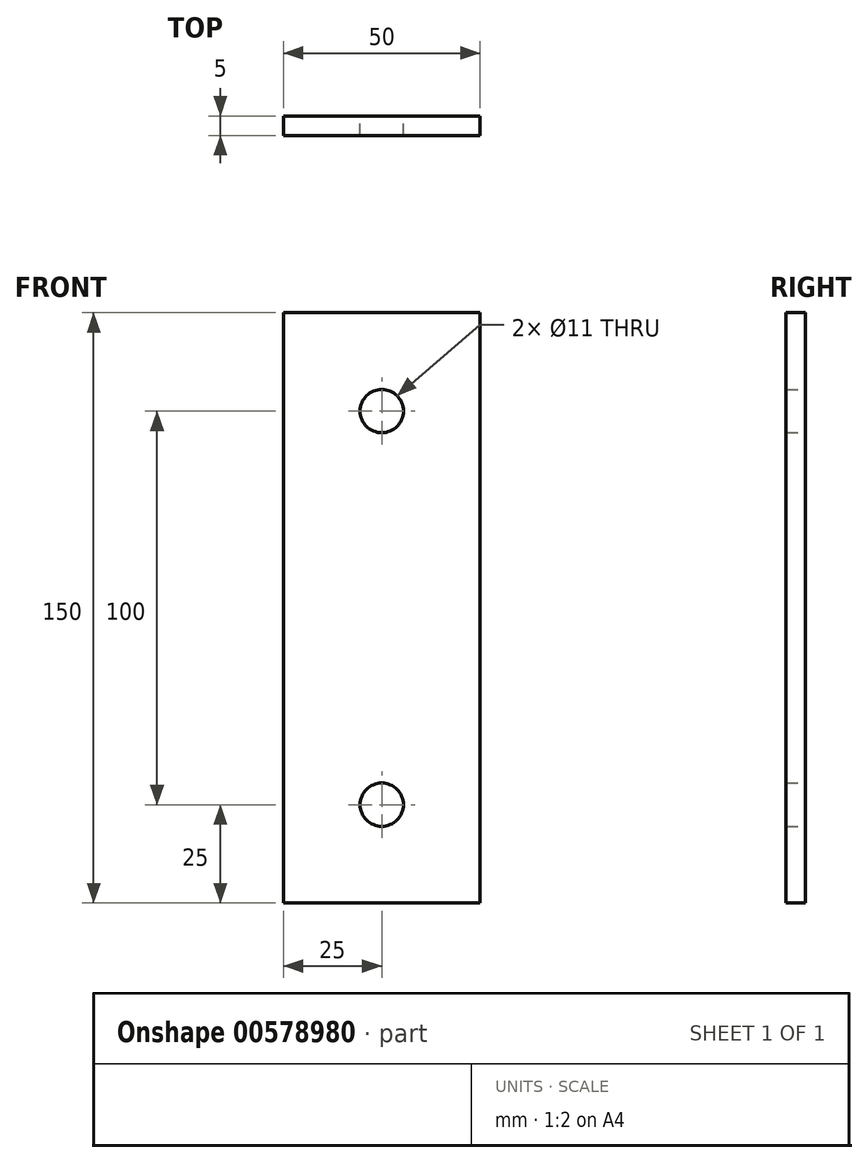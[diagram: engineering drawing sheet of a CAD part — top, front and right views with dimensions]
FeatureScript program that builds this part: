
annotation { "Feature Type Name" : "Feature", "Feature Type Description" : "" }
export const myFeature = defineFeature(function(context is Context, id is Id, definition is map)
    precondition{}
    {
        {
            var Q0;
            Q0=qCreatedBy(makeId("Front.planeOp"),FACE);
            var sketch = newSketch(context, id + "F0", { "sketchPlane" : qUnion([Q0])});
            skLineSegment(sketch, "E0.bottom", {"start": v(25, 75) * mm, "end": v(-25, 75) * mm});
            skLineSegment(sketch, "E0.top", {"start": v(25, -75) * mm, "end": v(-25, -75) * mm});
            skLineSegment(sketch, "E0.left", {"start": v(25, 75) * mm, "end": v(25, -75) * mm});
            skLineSegment(sketch, "E0.right", {"start": v(-25, 75) * mm, "end": v(-25, -75) * mm});
            skPoint(sketch, "E0.middle", {"position": v(0, 0) * mm});
            skCircle(sketch, "E1", {"center": v(0, -50) * mm, "radius": 5.5 * mm});
            skPoint(sketch, "E1.centerSnap0", {"position": v(0, -75) * mm});
            skCircle(sketch, "E2", {"center": v(0, 50) * mm, "radius": 5.5 * mm});
            skSolve(sketch);
        }
        {
            var Q0;
            Q0=makeQuery(id+"F0.imprint","IMPRINT",FACE,{"disambiguationData":[TD([[makeQuery(id+"F0.imprint","IMPRINT",EDGE,{"derivedFrom":sQuery(id+"F0.wireOp",EDGE,"E0.bottom")}),1.0]])]});
            extrude(context, id + "F1", {"entities" : qUnion([Q0]), "endBound" : BoundingType.SYMMETRIC, "depth" : 5 * mm, "offsetDistance" : 25 * mm});
        }
    });
